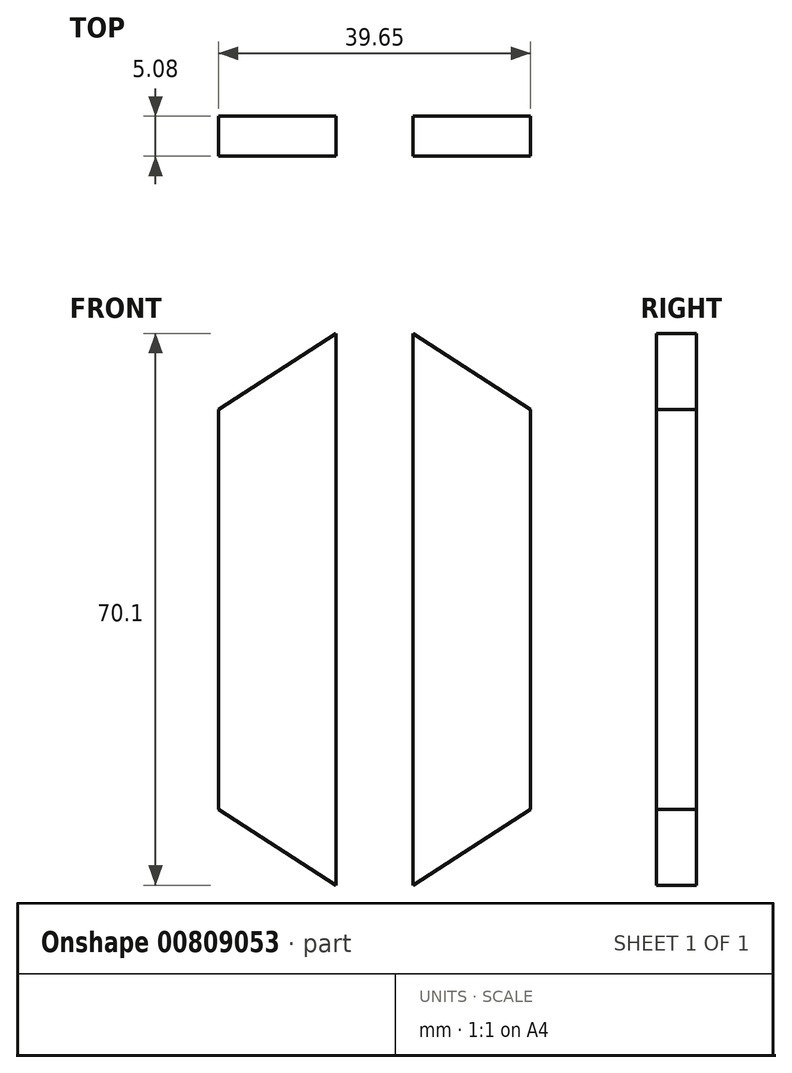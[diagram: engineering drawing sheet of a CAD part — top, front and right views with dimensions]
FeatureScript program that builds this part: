
annotation { "Feature Type Name" : "Feature", "Feature Type Description" : "" }
export const myFeature = defineFeature(function(context is Context, id is Id, definition is map)
    precondition{}
    {
        {
            var Q0;
            Q0=qCreatedBy(makeId("Front.planeOp"),FACE);
            var sketch = newSketch(context, id + "F0", { "sketchPlane" : qUnion([Q0])});
            skLineSegment(sketch, "E0", {"start": v(-45.7, 42.66) * mm, "end": v(-60.64, 33.01) * mm});
            skLineSegment(sketch, "E1", {"start": v(-60.64, 33.01) * mm, "end": v(-60.64, -17.79) * mm});
            skLineSegment(sketch, "E2", {"start": v(-60.64, -17.79) * mm, "end": v(-45.7, -27.44) * mm});
            skLineSegment(sketch, "E3", {"start": v(-45.7, -27.44) * mm, "end": v(-45.7, 42.66) * mm});
            skLineSegment(sketch, "E4", {"start": v(-35.92, 42.66) * mm, "end": v(-35.92, -27.44) * mm});
            skLineSegment(sketch, "E5", {"start": v(-35.92, -27.44) * mm, "end": v(-21, -17.79) * mm});
            skLineSegment(sketch, "E6", {"start": v(-21, -17.79) * mm, "end": v(-21, 33.01) * mm});
            skLineSegment(sketch, "E7", {"start": v(-21, 33.01) * mm, "end": v(-35.92, 42.66) * mm});
            skSolve(sketch);
        }
        {
            var Q0;
            Q0=makeQuery(id+"F0.imprint","IMPRINT",FACE,{"disambiguationData":[TD([[makeQuery(id+"F0.imprint","IMPRINT",EDGE,{"derivedFrom":sQuery(id+"F0.wireOp",EDGE,"E0")}),1.0]])]});
            var Q1;
            Q1=makeQuery(id+"F0.imprint","IMPRINT",FACE,{"disambiguationData":[TD([[makeQuery(id+"F0.imprint","IMPRINT",EDGE,{"derivedFrom":sQuery(id+"F0.wireOp",EDGE,"E4")}),1.0]])]});
            extrude(context, id + "F1", {"entities" : qUnion([Q0, Q1]), "depth" : 5.08 * mm, "offsetDistance" : 25.4 * mm});
        }
    });
